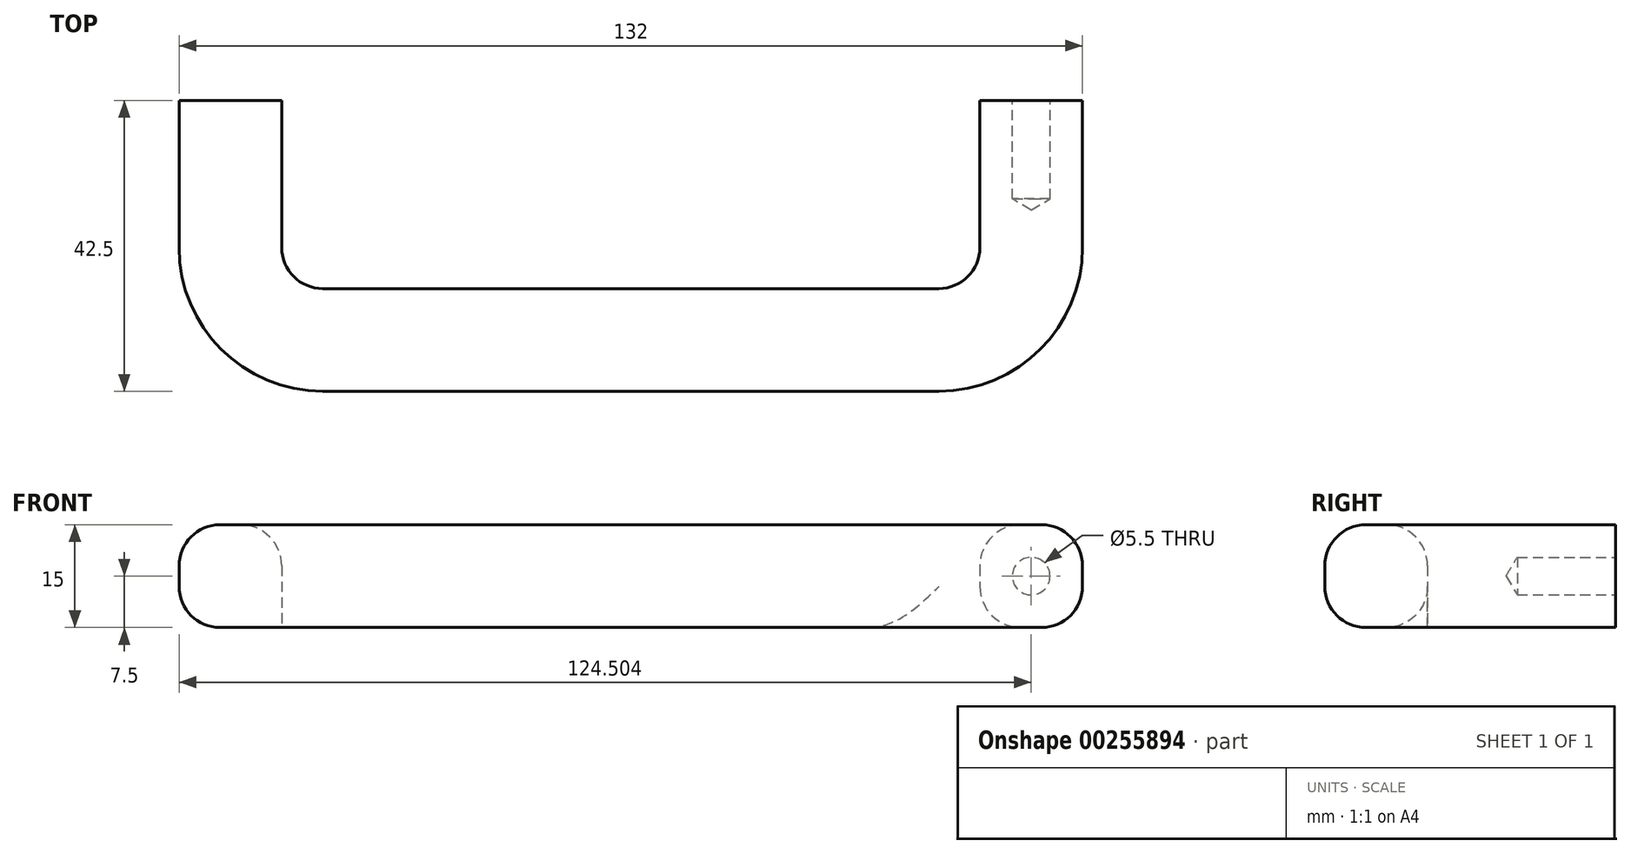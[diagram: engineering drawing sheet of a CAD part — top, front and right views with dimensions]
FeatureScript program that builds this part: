
annotation { "Feature Type Name" : "Feature", "Feature Type Description" : "" }
export const myFeature = defineFeature(function(context is Context, id is Id, definition is map)
    precondition{}
    {
        {
            var Q0;
            Q0=qCreatedBy(makeId("Top.planeOp"),FACE);
            var sketch = newSketch(context, id + "F0", { "sketchPlane" : qUnion([Q0])});
            skLineSegment(sketch, "E0", {"start": v(-88.54, 162.42) * mm, "end": v(-88.54, 134.92) * mm});
            skLineSegment(sketch, "E1", {"start": v(-124.74, 119.92) * mm, "end": v(28.46, 119.92) * mm});
            skLineSegment(sketch, "E2", {"start": v(28.46, 119.92) * mm, "end": v(28.46, 162.42) * mm});
            skLineSegment(sketch, "E3", {"start": v(-103.54, 162.42) * mm, "end": v(-88.54, 162.42) * mm});
            skLineSegment(sketch, "E4", {"start": v(-103.54, 162.42) * mm, "end": v(-103.54, 134.92) * mm});
            skLineSegment(sketch, "E5", {"start": v(-88.54, 134.92) * mm, "end": v(13.46, 134.92) * mm});
            skLineSegment(sketch, "E6", {"start": v(13.46, 134.92) * mm, "end": v(13.46, 162.42) * mm});
            skLineSegment(sketch, "E7", {"start": v(13.46, 162.42) * mm, "end": v(28.46, 162.42) * mm});
            skLineSegment(sketch, "E8", {"start": v(-96.04, 162.42) * mm, "end": v(-96.04, 127.42) * mm, "construction": true});
            skLineSegment(sketch, "E9", {"start": v(-96.04, 127.42) * mm, "end": v(20.96, 127.42) * mm, "construction": true});
            skLineSegment(sketch, "E10", {"start": v(20.96, 127.42) * mm, "end": v(20.96, 162.42) * mm, "construction": true});
            skLineSegment(sketch, "E11", {"start": v(28.46, 119.92) * mm, "end": v(13.46, 134.92) * mm, "construction": true});
            skLineSegment(sketch, "E12", {"start": v(-103.54, 134.92) * mm, "end": v(-103.54, 119.92) * mm});
            skLineSegment(sketch, "E13", {"start": v(-124.74, 119.92) * mm, "end": v(-103.54, 119.92) * mm});
            skSolve(sketch);
        }
        {
            var Q0;
            Q0=makeQuery(id+"F0.imprint","IMPRINT",FACE,{"disambiguationData":[TD([[makeQuery(id+"F0.imprint","IMPRINT",EDGE,{"derivedFrom":sQuery(id+"F0.wireOp",EDGE,"E0")}),-1.0]])]});
            extrude(context, id + "F1", {"entities" : qUnion([Q0]), "depth" : 15 * mm});
        }
        {
            var Q0;
            Q0=makeQuery(id+"F1.opExtrude","CAP_EDGE",EDGE,{"disambiguationData":[OSD([sQuery(id+"F0.wireOp",EDGE,"E1"),sQuery(id+"F0.wireOp",EDGE,"E13")])],"isStart":false});
            var Q1;
            Q1=makeQuery(id+"F1.opExtrude","CAP_EDGE",EDGE,{"disambiguationData":[OSD([sQuery(id+"F0.wireOp",EDGE,"E5")])],"isStart":false});
            var Q2;
            Q2=makeQuery(id+"F1.opExtrude","CAP_EDGE",EDGE,{"disambiguationData":[OSD([sQuery(id+"F0.wireOp",EDGE,"E6")])],"isStart":false});
            var Q3;
            Q3=makeQuery(id+"F1.opExtrude","CAP_EDGE",EDGE,{"disambiguationData":[OSD([sQuery(id+"F0.wireOp",EDGE,"E6")])],"isStart":true});
            var Q4;
            Q4=makeQuery(id+"F1.opExtrude","CAP_EDGE",EDGE,{"disambiguationData":[OSD([sQuery(id+"F0.wireOp",EDGE,"E0")])],"isStart":false});
            var Q5;
            Q5=makeQuery(id+"F1.opExtrude","CAP_EDGE",EDGE,{"disambiguationData":[OSD([sQuery(id+"F0.wireOp",EDGE,"E4"),sQuery(id+"F0.wireOp",EDGE,"E12")])],"isStart":false});
            var Q6;
            Q6=makeQuery(id+"F1.opExtrude","CAP_EDGE",EDGE,{"disambiguationData":[OSD([sQuery(id+"F0.wireOp",EDGE,"E4"),sQuery(id+"F0.wireOp",EDGE,"E12")])],"isStart":true});
            var Q7;
            Q7=makeQuery(id+"F1.opExtrude","SWEPT_EDGE",EDGE,{"disambiguationData":[OSD([sQuery(id+"F0.wireOp",EDGE,"E0"),sQuery(id+"F0.wireOp",EDGE,"E5")])]});
            var Q8;
            Q8=makeQuery(id+"F1.opExtrude","SWEPT_EDGE",EDGE,{"disambiguationData":[OSD([sQuery(id+"F0.wireOp",EDGE,"E5"),sQuery(id+"F0.wireOp",EDGE,"E6")])]});
            var Q9;
            Q9=makeQuery(id+"F1.opExtrude","CAP_EDGE",EDGE,{"disambiguationData":[OSD([sQuery(id+"F0.wireOp",EDGE,"E2")])],"isStart":true});
            var Q10;
            Q10=makeQuery(id+"F1.opExtrude","CAP_EDGE",EDGE,{"disambiguationData":[OSD([sQuery(id+"F0.wireOp",EDGE,"E2")])],"isStart":false});
            var Q11;
            Q11=makeQuery(id+"F1.opExtrude","CAP_EDGE",EDGE,{"disambiguationData":[OSD([sQuery(id+"F0.wireOp",EDGE,"E1"),sQuery(id+"F0.wireOp",EDGE,"E13")])],"isStart":true});
            fillet(context, id + "F2", {"entities" : qUnion([Q0, Q1, Q2, Q3, Q4, Q5, Q6, Q7, Q8, Q9, Q10, Q11]), "radius" : 6 * mm, "tangentPropagation" : true, "allowEdgeOverflow" : false});
        }
        {
            var Q0;
            Q0=makeQuery(id+"F1.opExtrude","SWEPT_EDGE",EDGE,{"disambiguationData":[OSD([sQuery(id+"F0.wireOp",EDGE,"E12"),sQuery(id+"F0.wireOp",EDGE,"E13")])]});
            var Q1;
            Q1=makeQuery(id+"F1.opExtrude","SWEPT_EDGE",EDGE,{"disambiguationData":[OSD([sQuery(id+"F0.wireOp",EDGE,"E1"),sQuery(id+"F0.wireOp",EDGE,"E2")])]});
            fillet(context, id + "F3", {"entities" : qUnion([Q0, Q1]), "radius" : 21 * mm, "tangentPropagation" : true, "allowEdgeOverflow" : false});
        }
        {
            var Q0;
            Q0=makeQuery(id+"F1.opExtrude","SWEPT_FACE",FACE,{"disambiguationData":[OSD([sQuery(id+"F0.wireOp",EDGE,"E3")])]});
            var sketch = newSketch(context, id + "F4", { "sketchPlane" : qUnion([Q0])});
            skPoint(sketch, "E14", {"position": v(-20.96, 7.5) * mm});
            skPoint(sketch, "E15", {"position": v(129.04, 7.5) * mm});
            skSolve(sketch);
        }
        {
            var Q0;
            Q0=sQuery(id+"F4.wireOp",VERTEX,"E14");
            var Q1;
            Q1=sQuery(id+"F4.wireOp",VERTEX,"E15");
            var Q2;
            Q2=makeQuery(id+"F1.opExtrude","SWEPT_BODY",BODY,{"disambiguationData":[OSD([sQuery(id+"F0.wireOp",EDGE,"E0"),sQuery(id+"F0.wireOp",EDGE,"E1"),sQuery(id+"F0.wireOp",EDGE,"E2"),sQuery(id+"F0.wireOp",EDGE,"E3"),sQuery(id+"F0.wireOp",EDGE,"E4"),sQuery(id+"F0.wireOp",EDGE,"E5"),sQuery(id+"F0.wireOp",EDGE,"E6"),sQuery(id+"F0.wireOp",EDGE,"E7"),sQuery(id+"F0.wireOp",EDGE,"E12"),sQuery(id+"F0.wireOp",EDGE,"E13")])]});
            hole(context, id + "F5", {"style" : HoleStyle.SIMPLE, "endStyle" : HoleEndStyle.BLIND, "standardTappedOrClearance" : lookupTablePath({ "standard" : "ISO", "fit" : "Normal", "size" : "M5", "type" : "Clearance" }), "standardBlindInLast" : lookupTablePath({ "fit" : "Standard", "standard" : "ISO", "size" : "M5", "type" : "Clearance" }), "holeDiameter" : 5.5 * mm, "holeDepth" : 14.4 * mm, "tappedDepth" : 12 * mm, "tapClearance" : 3, "startFromSketch" : true, "locations" : qUnion([Q0, Q1]), "scope" : qUnion([Q2])});
        }
    });
